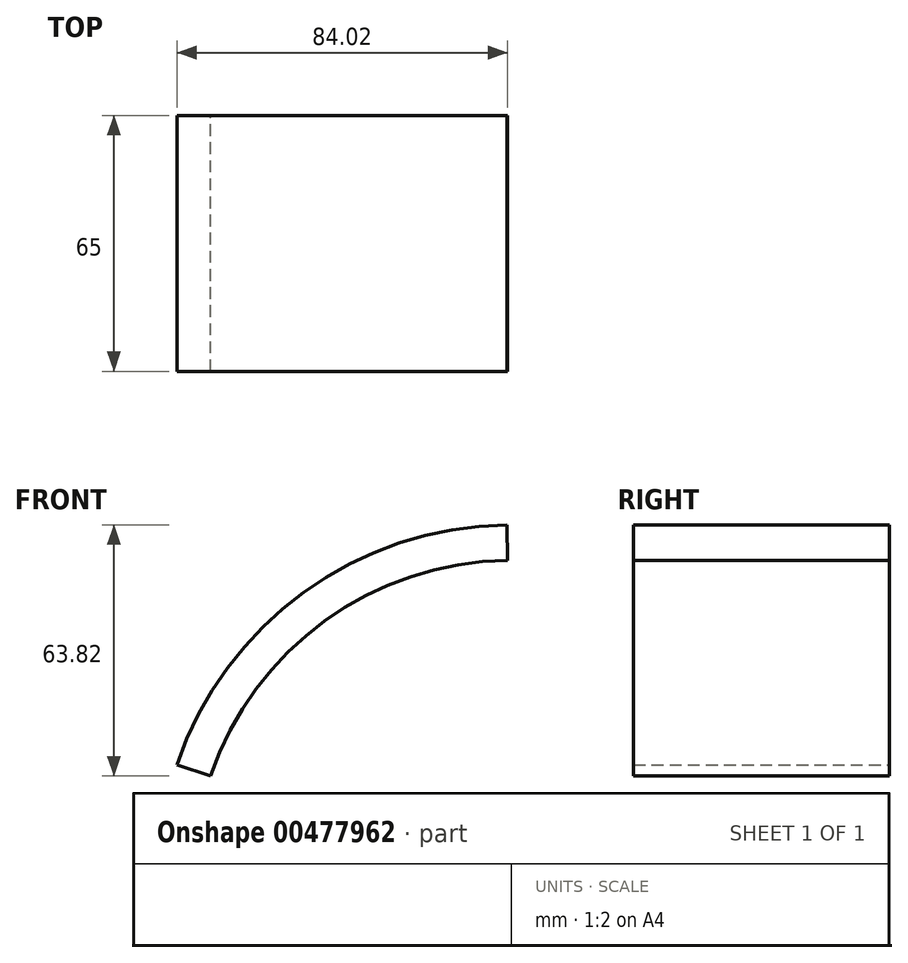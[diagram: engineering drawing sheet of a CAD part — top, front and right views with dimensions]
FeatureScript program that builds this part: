
annotation { "Feature Type Name" : "Feature", "Feature Type Description" : "" }
export const myFeature = defineFeature(function(context is Context, id is Id, definition is map)
    precondition{}
    {
        {
            var Q0;
            Q0=qCreatedBy(makeId("Front.planeOp"),FACE);
            var sketch = newSketch(context, id + "F0", { "sketchPlane" : qUnion([Q0])});
            skArc(sketch, "E0", {"start": v(-1.02, 80.74) * mm, "mid": v(-47.46, 65.33) * mm, "end": v(-76.48, 25.92) * mm});
            skArc(sketch, "E1", {"start": v(-1.13, 89.74) * mm, "mid": v(-52.8, 72.58) * mm, "end": v(-85.04, 28.7) * mm});
            skLineSegment(sketch, "E2", {"start": v(-1.02, 80.74) * mm, "end": v(-1.13, 89.74) * mm});
            skLineSegment(sketch, "E3", {"start": v(0, 0) * mm, "end": v(0, 105.8) * mm, "construction": true});
            skLineSegment(sketch, "E4.0", {"start": v(-1.02, 0) * mm, "end": v(-1.02, 105.8) * mm, "construction": true});
            skLineSegment(sketch, "E5", {"start": v(0, 0) * mm, "end": v(-100.24, 32.57) * mm, "construction": true});
            skLineSegment(sketch, "E6", {"start": v(-85.04, 28.7) * mm, "end": v(-76.48, 25.92) * mm});
            skSolve(sketch);
        }
        {
            var Q0;
            Q0=makeQuery(id+"F0.imprint","IMPRINT",FACE,{"disambiguationData":[TD([[makeQuery(id+"F0.imprint","IMPRINT",EDGE,{"derivedFrom":sQuery(id+"F0.wireOp",EDGE,"E0")}),-1.0]])]});
            extrude(context, id + "F1", {"entities" : qUnion([Q0]), "depth" : 65 * mm});
        }
    });
